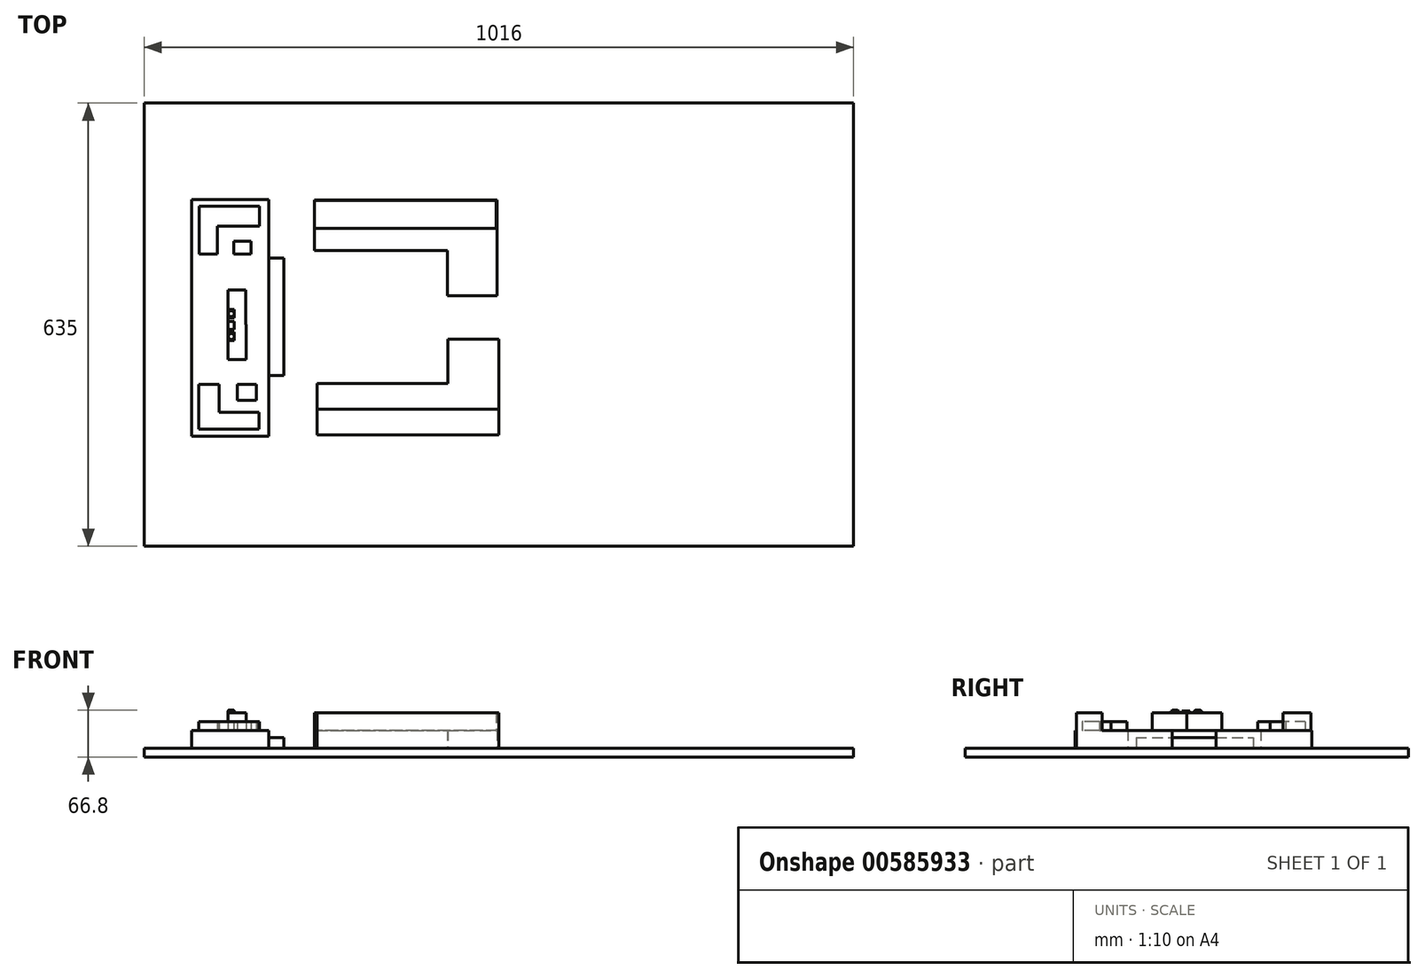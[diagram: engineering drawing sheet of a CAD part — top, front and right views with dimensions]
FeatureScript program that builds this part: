
annotation { "Feature Type Name" : "Feature", "Feature Type Description" : "" }
export const myFeature = defineFeature(function(context is Context, id is Id, definition is map)
    precondition{}
    {
        {
            var Q0;
            Q0=qCreatedBy(makeId("Top.planeOp"),FACE);
            var sketch = newSketch(context, id + "F0", { "sketchPlane" : qUnion([Q0])});
            skLineSegment(sketch, "E0.bottom", {"start": v(508, -317.5) * mm, "end": v(-508, -317.5) * mm});
            skLineSegment(sketch, "E0.top", {"start": v(508, 317.5) * mm, "end": v(-508, 317.5) * mm});
            skLineSegment(sketch, "E0.left", {"start": v(508, -317.5) * mm, "end": v(508, 317.5) * mm});
            skLineSegment(sketch, "E0.right", {"start": v(-508, -317.5) * mm, "end": v(-508, 317.5) * mm});
            skSolve(sketch);
        }
        {
            var Q0;
            Q0 = qSketchRegion(id + "F0", true);
            extrude(context, id + "F1", {"entities" : qUnion([Q0]), "oppositeDirection" : true, "depth" : 12.7 * mm, "offsetDistance" : 25.4 * mm});
        }
        {
            var Q0;
            Q0=makeQuery(id+"F1.opExtrude","CAP_FACE",FACE,{"disambiguationData":[OSD([sQuery(id+"F0.wireOp",EDGE,"E0.bottom"),sQuery(id+"F0.wireOp",EDGE,"E0.top"),sQuery(id+"F0.wireOp",EDGE,"E0.left"),sQuery(id+"F0.wireOp",EDGE,"E0.right")])],"isStart":true});
            var sketch = newSketch(context, id + "F2", { "sketchPlane" : qUnion([Q0])});
            skLineSegment(sketch, "E1.bottom", {"start": v(-329.78, -159.84) * mm, "end": v(-440.25, -159.84) * mm});
            skLineSegment(sketch, "E1.top", {"start": v(-329.78, 178.99) * mm, "end": v(-440.25, 178.99) * mm});
            skLineSegment(sketch, "E1.left", {"start": v(-329.78, -159.84) * mm, "end": v(-329.78, 178.99) * mm});
            skLineSegment(sketch, "E1.right", {"start": v(-440.25, -159.84) * mm, "end": v(-440.25, 178.99) * mm});
            skLineSegment(sketch, "E2.bottom", {"start": v(-260.44, -158) * mm, "end": v(-72.75, -158) * mm});
            skLineSegment(sketch, "E2.top", {"start": v(-260.44, -84.58) * mm, "end": v(-72.75, -84.58) * mm});
            skLineSegment(sketch, "E2.left", {"start": v(-260.44, -158) * mm, "end": v(-260.44, -84.58) * mm});
            skLineSegment(sketch, "E2.right", {"start": v(-72.75, -158) * mm, "end": v(-72.75, -84.58) * mm});
            skLineSegment(sketch, "E3.bottom", {"start": v(-264.32, 106.03) * mm, "end": v(-73.41, 106.03) * mm});
            skLineSegment(sketch, "E3.top", {"start": v(-264.32, 178.7) * mm, "end": v(-73.41, 178.7) * mm});
            skLineSegment(sketch, "E3.left", {"start": v(-264.32, 106.03) * mm, "end": v(-264.32, 178.7) * mm});
            skLineSegment(sketch, "E3.right", {"start": v(-73.41, 106.03) * mm, "end": v(-73.41, 178.7) * mm});
            skLineSegment(sketch, "E4.bottom", {"start": v(-72.75, -158) * mm, "end": v(0, -158) * mm});
            skLineSegment(sketch, "E4.top", {"start": v(-72.75, -20.85) * mm, "end": v(0, -20.85) * mm});
            skLineSegment(sketch, "E4.left", {"start": v(-72.75, -158) * mm, "end": v(-72.75, -20.85) * mm});
            skLineSegment(sketch, "E4.right", {"start": v(0, -158) * mm, "end": v(0, -20.85) * mm});
            skLineSegment(sketch, "E5.bottom", {"start": v(-73.41, 41.72) * mm, "end": v(-2.68, 41.72) * mm});
            skLineSegment(sketch, "E5.top", {"start": v(-73.41, 178.88) * mm, "end": v(-2.68, 178.88) * mm});
            skLineSegment(sketch, "E5.left", {"start": v(-73.41, 41.72) * mm, "end": v(-73.41, 178.88) * mm});
            skLineSegment(sketch, "E5.right", {"start": v(-2.68, 41.72) * mm, "end": v(-2.68, 178.88) * mm});
            skSolve(sketch);
        }
        {
            var Q0;
            {var subQ3=sQuery(id+"F2.wireOp",EDGE,"E5.bottom");Q0=makeQuery(id+"F2.imprint","IMPRINT",FACE,{"disambiguationData":[TD([[makeQuery(id+"F2.imprint","IMPRINT",EDGE,{"derivedFrom":subQ3}),1.0]])]});}
            var Q1;
            {var subQ0=sQuery(id+"F2.wireOp",EDGE,"E3.bottom");Q1=makeQuery(id+"F2.imprint","IMPRINT",FACE,{"disambiguationData":[TD([[makeQuery(id+"F2.imprint","IMPRINT",EDGE,{"derivedFrom":subQ0}),1.0]])]});}
            var Q2;
            Q2 = qSketchRegion(id + "F2", true);
            extrude(context, id + "F3", {"entities" : qUnion([Q0, Q1, Q2]), "operationType" : NewBodyOperationType.ADD, "depth" : 25.4 * mm, "offsetDistance" : 25.4 * mm});
        }
        {
            var Q0;
            Q0=makeQuery(id+"F3.opExtrude","CAP_FACE",FACE,{"disambiguationData":[OSD([sQuery(id+"F2.wireOp",EDGE,"E2.bottom"),sQuery(id+"F2.wireOp",EDGE,"E2.top"),sQuery(id+"F2.wireOp",EDGE,"E2.left"),sQuery(id+"F2.wireOp",EDGE,"E4.bottom"),sQuery(id+"F2.wireOp",EDGE,"E4.top"),sQuery(id+"F2.wireOp",EDGE,"E4.left"),sQuery(id+"F2.wireOp",EDGE,"E4.right")])],"isStart":false});
            var sketch = newSketch(context, id + "F4", { "sketchPlane" : qUnion([Q0])});
            skLineSegment(sketch, "E6.bottom", {"start": v(0, -158) * mm, "end": v(-260.44, -158) * mm});
            skLineSegment(sketch, "E6.top", {"start": v(0, -121.3) * mm, "end": v(-260.44, -121.3) * mm});
            skLineSegment(sketch, "E6.left", {"start": v(0, -158) * mm, "end": v(0, -121.3) * mm});
            skLineSegment(sketch, "E6.right", {"start": v(-260.44, -158) * mm, "end": v(-260.44, -121.3) * mm});
            skLineSegment(sketch, "E7.bottom", {"start": v(-3.63, 137.69) * mm, "end": v(-264.07, 137.69) * mm});
            skLineSegment(sketch, "E7.top", {"start": v(-3.63, 177.67) * mm, "end": v(-264.07, 177.67) * mm});
            skLineSegment(sketch, "E7.left", {"start": v(-3.63, 137.69) * mm, "end": v(-3.63, 177.67) * mm});
            skLineSegment(sketch, "E7.right", {"start": v(-264.07, 137.69) * mm, "end": v(-264.07, 177.67) * mm});
            skLineSegment(sketch, "E8.bottom", {"start": v(-362.47, 0) * mm, "end": v(-387.96, 0) * mm});
            skLineSegment(sketch, "E8.top", {"start": v(-362.47, 49.88) * mm, "end": v(-387.96, 49.88) * mm});
            skLineSegment(sketch, "E8.left", {"start": v(-362.47, 0) * mm, "end": v(-362.47, 49.88) * mm});
            skLineSegment(sketch, "E8.right", {"start": v(-387.96, 0) * mm, "end": v(-387.96, 49.88) * mm});
            skLineSegment(sketch, "E9.bottom", {"start": v(-362.27, -49.75) * mm, "end": v(-387.77, -49.75) * mm});
            skLineSegment(sketch, "E9.top", {"start": v(-362.27, 0.13) * mm, "end": v(-387.77, 0.13) * mm});
            skLineSegment(sketch, "E9.left", {"start": v(-362.27, -49.75) * mm, "end": v(-362.27, 0.13) * mm});
            skLineSegment(sketch, "E9.right", {"start": v(-387.77, -49.75) * mm, "end": v(-387.77, 0.13) * mm});
            skSolve(sketch);
        }
        {
            var Q0;
            Q0 = qSketchRegion(id + "F4", true);
            extrude(context, id + "F5", {"entities" : qUnion([Q0]), "operationType" : NewBodyOperationType.ADD, "depth" : 25.4 * mm, "offsetDistance" : 25.4 * mm});
        }
        {
            var Q0;
            Q0=makeQuery(id+"F3.opExtrude","CAP_FACE",FACE,{"disambiguationData":[OSD([sQuery(id+"F2.wireOp",EDGE,"E1.bottom"),sQuery(id+"F2.wireOp",EDGE,"E1.top"),sQuery(id+"F2.wireOp",EDGE,"E1.left"),sQuery(id+"F2.wireOp",EDGE,"E1.right")])],"isStart":false});
            var sketch = newSketch(context, id + "F6", { "sketchPlane" : qUnion([Q0])});
            skLineSegment(sketch, "E10.bottom", {"start": v(-343.37, -125.34) * mm, "end": v(-429.92, -125.34) * mm});
            skLineSegment(sketch, "E10.top", {"start": v(-343.37, -149.68) * mm, "end": v(-429.92, -149.68) * mm});
            skLineSegment(sketch, "E10.left", {"start": v(-343.37, -125.34) * mm, "end": v(-343.37, -149.68) * mm});
            skLineSegment(sketch, "E10.right", {"start": v(-429.92, -125.34) * mm, "end": v(-429.92, -149.68) * mm});
            skLineSegment(sketch, "E11.bottom", {"start": v(-400.92, -125.34) * mm, "end": v(-429.92, -125.34) * mm});
            skLineSegment(sketch, "E11.top", {"start": v(-400.92, -85.81) * mm, "end": v(-429.92, -85.81) * mm});
            skLineSegment(sketch, "E11.left", {"start": v(-400.92, -125.34) * mm, "end": v(-400.92, -85.81) * mm});
            skLineSegment(sketch, "E11.right", {"start": v(-429.92, -125.34) * mm, "end": v(-429.92, -85.81) * mm});
            skLineSegment(sketch, "E12.bottom", {"start": v(-347.54, -85.81) * mm, "end": v(-374.44, -85.81) * mm});
            skLineSegment(sketch, "E12.top", {"start": v(-347.54, -108.62) * mm, "end": v(-374.44, -108.62) * mm});
            skLineSegment(sketch, "E12.left", {"start": v(-347.54, -85.81) * mm, "end": v(-347.54, -108.62) * mm});
            skLineSegment(sketch, "E12.right", {"start": v(-374.44, -85.81) * mm, "end": v(-374.44, -108.62) * mm});
            skLineSegment(sketch, "E13.bottom", {"start": v(-342.87, 169.86) * mm, "end": v(-429.58, 169.86) * mm});
            skLineSegment(sketch, "E13.top", {"start": v(-342.87, 141.4) * mm, "end": v(-429.58, 141.4) * mm});
            skLineSegment(sketch, "E13.left", {"start": v(-342.87, 169.86) * mm, "end": v(-342.87, 141.4) * mm});
            skLineSegment(sketch, "E13.right", {"start": v(-429.58, 169.86) * mm, "end": v(-429.58, 141.4) * mm});
            skLineSegment(sketch, "E14.bottom", {"start": v(-403.04, 141.4) * mm, "end": v(-429.58, 141.4) * mm});
            skLineSegment(sketch, "E14.top", {"start": v(-403.04, 101.33) * mm, "end": v(-429.58, 101.33) * mm});
            skLineSegment(sketch, "E14.left", {"start": v(-403.04, 141.4) * mm, "end": v(-403.04, 101.33) * mm});
            skLineSegment(sketch, "E14.right", {"start": v(-429.58, 141.4) * mm, "end": v(-429.58, 101.33) * mm});
            skLineSegment(sketch, "E15.bottom", {"start": v(-354.87, 119.32) * mm, "end": v(-380, 119.32) * mm});
            skLineSegment(sketch, "E15.top", {"start": v(-354.87, 101.33) * mm, "end": v(-380, 101.33) * mm});
            skLineSegment(sketch, "E15.left", {"start": v(-354.87, 119.32) * mm, "end": v(-354.87, 101.33) * mm});
            skLineSegment(sketch, "E15.right", {"start": v(-380, 119.32) * mm, "end": v(-380, 101.33) * mm});
            skSolve(sketch);
        }
        {
            var Q0;
            Q0 = qSketchRegion(id + "F6", true);
            extrude(context, id + "F7", {"entities" : qUnion([Q0]), "operationType" : NewBodyOperationType.ADD, "depth" : 12.7 * mm, "offsetDistance" : 25.4 * mm});
        }
        {
            var Q0;
            Q0=makeQuery(id+"F5.opExtrude","CAP_FACE",FACE,{"disambiguationData":[OSD([sQuery(id+"F4.wireOp",EDGE,"E8.bottom"),sQuery(id+"F4.wireOp",EDGE,"E8.top"),sQuery(id+"F4.wireOp",EDGE,"E8.left"),sQuery(id+"F4.wireOp",EDGE,"E8.right"),sQuery(id+"F4.wireOp",EDGE,"E9.bottom"),sQuery(id+"F4.wireOp",EDGE,"E9.top"),sQuery(id+"F4.wireOp",EDGE,"E9.left"),sQuery(id+"F4.wireOp",EDGE,"E9.right")])],"isStart":false});
            var sketch = newSketch(context, id + "F8", { "sketchPlane" : qUnion([Q0])});
            skLineSegment(sketch, "E16.bottom", {"start": v(-378.82, 4.5) * mm, "end": v(-387.77, 4.5) * mm});
            skLineSegment(sketch, "E16.top", {"start": v(-378.82, -6.86) * mm, "end": v(-387.77, -6.86) * mm});
            skLineSegment(sketch, "E16.left", {"start": v(-378.82, 4.5) * mm, "end": v(-378.82, -6.86) * mm});
            skLineSegment(sketch, "E16.right", {"start": v(-387.77, 4.5) * mm, "end": v(-387.77, -6.86) * mm});
            skLineSegment(sketch, "E17.bottom", {"start": v(-387.96, 9.85) * mm, "end": v(-379.03, 9.85) * mm});
            skLineSegment(sketch, "E17.top", {"start": v(-387.96, 21.5) * mm, "end": v(-379.03, 21.5) * mm});
            skLineSegment(sketch, "E17.left", {"start": v(-387.96, 9.85) * mm, "end": v(-387.96, 21.5) * mm});
            skLineSegment(sketch, "E17.right", {"start": v(-379.03, 9.85) * mm, "end": v(-379.03, 21.5) * mm});
            skLineSegment(sketch, "E18.bottom", {"start": v(-379.03, -10.8) * mm, "end": v(-387.77, -10.8) * mm});
            skLineSegment(sketch, "E18.top", {"start": v(-379.03, -22.93) * mm, "end": v(-387.77, -22.93) * mm});
            skLineSegment(sketch, "E18.left", {"start": v(-379.03, -10.8) * mm, "end": v(-379.03, -22.93) * mm});
            skLineSegment(sketch, "E18.right", {"start": v(-387.77, -10.8) * mm, "end": v(-387.77, -22.93) * mm});
            skSolve(sketch);
        }
        {
            var Q0;
            Q0 = qSketchRegion(id + "F8", true);
            extrude(context, id + "F9", {"entities" : qUnion([Q0]), "operationType" : NewBodyOperationType.ADD, "depth" : 2.54 * mm, "offsetDistance" : 25.4 * mm});
        }
        {
            var Q0;
            Q0=makeQuery(id+"F9.opExtrude","CAP_FACE",FACE,{"disambiguationData":[OSD([sQuery(id+"F8.wireOp",EDGE,"E18.bottom"),sQuery(id+"F8.wireOp",EDGE,"E18.top"),sQuery(id+"F8.wireOp",EDGE,"E18.left"),sQuery(id+"F8.wireOp",EDGE,"E18.right")])],"isStart":false});
            var sketch = newSketch(context, id + "F10", { "sketchPlane" : qUnion([Q0])});
            skCircle(sketch, "E19", {"center": v(-383.34, -17) * mm, "radius": 4.17 * mm});
            skCircle(sketch, "E20", {"center": v(-383.4, 15.77) * mm, "radius": 4.27 * mm});
            skPoint(sketch, "E20.centerSnap0", {"position": v(-383.4, -10.8) * mm});
            skSolve(sketch);
        }
        {
            var Q0;
            Q0 = qSketchRegion(id + "F10", true);
            extrude(context, id + "F11", {"entities" : qUnion([Q0]), "operationType" : NewBodyOperationType.ADD, "depth" : 0.76 * mm, "offsetDistance" : 25.4 * mm});
        }
        {
            var Q0;
            Q0=makeQuery(id+"F11.opExtrude","CAP_EDGE",EDGE,{"disambiguationData":[OSD([sQuery(id+"F10.wireOp",EDGE,"E19")])],"isStart":false});
            var Q1;
            Q1=makeQuery(id+"F11.opExtrude","CAP_EDGE",EDGE,{"disambiguationData":[OSD([sQuery(id+"F10.wireOp",EDGE,"E20")])],"isStart":false});
            fillet(context, id + "F12", {"entities" : qUnion([Q0, Q1]), "radius" : 0.76 * mm, "tangentPropagation" : true, "allowEdgeOverflow" : false});
        }
        {
            var Q0;
            Q0=makeQuery(id+"F1.opExtrude","CAP_FACE",FACE,{"disambiguationData":[OSD([sQuery(id+"F0.wireOp",EDGE,"E0.bottom"),sQuery(id+"F0.wireOp",EDGE,"E0.top"),sQuery(id+"F0.wireOp",EDGE,"E0.left"),sQuery(id+"F0.wireOp",EDGE,"E0.right")])],"isStart":true});
            var sketch = newSketch(context, id + "F13", { "sketchPlane" : qUnion([Q0])});
            skLineSegment(sketch, "E21.bottom", {"start": v(-307.9, -72.57) * mm, "end": v(-329.78, -72.57) * mm});
            skLineSegment(sketch, "E21.top", {"start": v(-307.9, 95.32) * mm, "end": v(-329.78, 95.32) * mm});
            skLineSegment(sketch, "E21.left", {"start": v(-307.9, -72.57) * mm, "end": v(-307.9, 95.32) * mm});
            skLineSegment(sketch, "E21.right", {"start": v(-329.78, -72.57) * mm, "end": v(-329.78, 95.32) * mm});
            skSolve(sketch);
        }
        {
            var Q0;
            Q0 = qSketchRegion(id + "F13", true);
            extrude(context, id + "F14", {"entities" : qUnion([Q0]), "operationType" : NewBodyOperationType.ADD, "depth" : 15.24 * mm, "offsetDistance" : 25.4 * mm});
        }
    });
